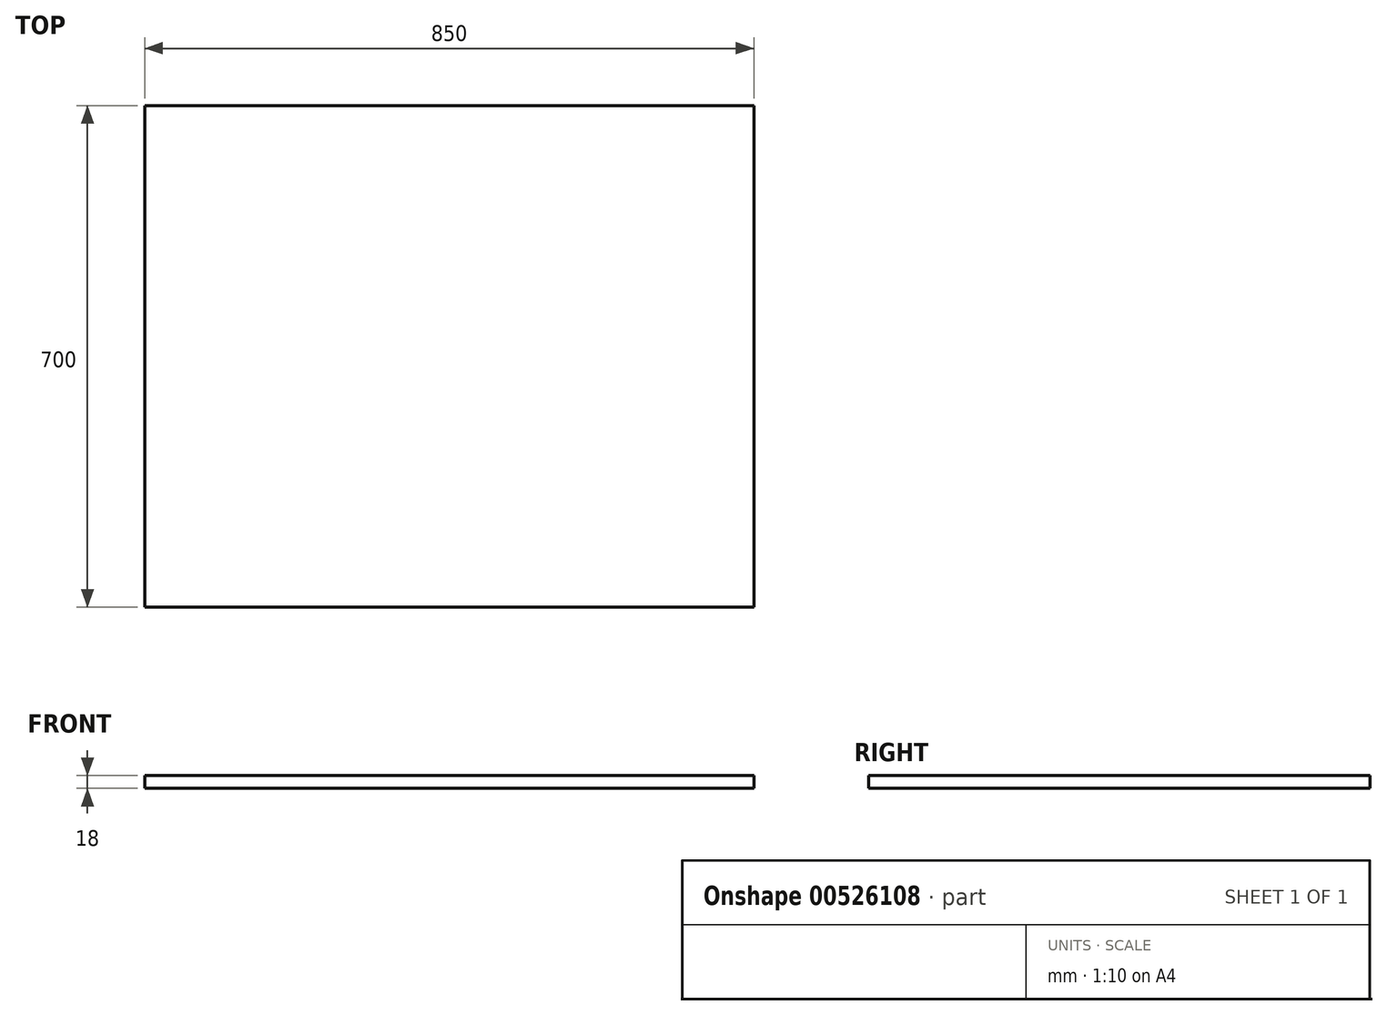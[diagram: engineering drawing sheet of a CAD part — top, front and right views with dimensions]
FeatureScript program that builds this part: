
annotation { "Feature Type Name" : "Feature", "Feature Type Description" : "" }
export const myFeature = defineFeature(function(context is Context, id is Id, definition is map)
    precondition{}
    {
        {
            var Q0;
            Q0=qCreatedBy(makeId("Top.planeOp"),FACE);
            var sketch = newSketch(context, id + "F0", { "sketchPlane" : qUnion([Q0])});
            skLineSegment(sketch, "E0.bottom", {"start": v(425, 350) * mm, "end": v(-425, 350) * mm});
            skLineSegment(sketch, "E0.top", {"start": v(425, -350) * mm, "end": v(-425, -350) * mm});
            skLineSegment(sketch, "E0.left", {"start": v(425, 350) * mm, "end": v(425, -350) * mm});
            skLineSegment(sketch, "E0.right", {"start": v(-425, 350) * mm, "end": v(-425, -350) * mm});
            skPoint(sketch, "E0.middle", {"position": v(0, 0) * mm});
            skSolve(sketch);
        }
        {
            var Q0;
            Q0=qSketchRegion(id+"F0",true);
            extrude(context, id + "F1", {"entities" : qUnion([Q0]), "depth" : 18 * mm, "offsetDistance" : 25 * mm});
        }
    });
